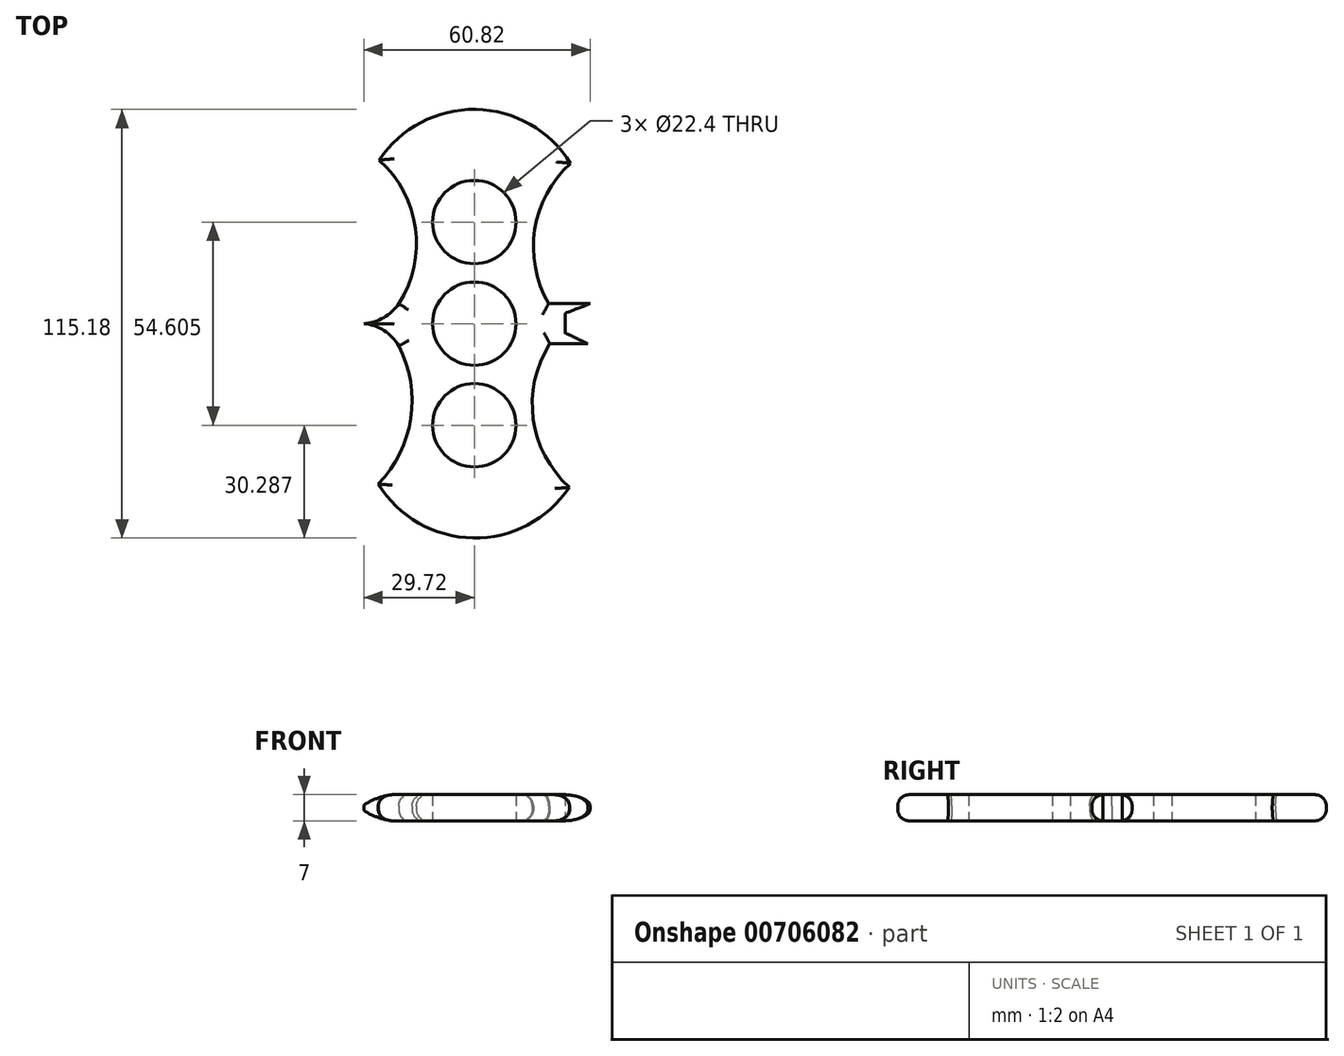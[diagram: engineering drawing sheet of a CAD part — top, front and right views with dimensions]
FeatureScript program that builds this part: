
annotation { "Feature Type Name" : "Feature", "Feature Type Description" : "" }
export const myFeature = defineFeature(function(context is Context, id is Id, definition is map)
    precondition{}
    {
        {
            var Q0;
            Q0=qCreatedBy(makeId("Top.planeOp"),FACE);
            var sketch = newSketch(context, id + "F0", { "sketchPlane" : qUnion([Q0])});
            skCircle(sketch, "E0", {"center": v(0, 0) * mm, "radius": 11.2 * mm});
            skCircle(sketch, "E1", {"center": v(0, 27.3) * mm, "radius": 11.2 * mm});
            skCircle(sketch, "E2.1.0", {"center": v(0, -27.3) * mm, "radius": 11.2 * mm});
            skArc(sketch, "E3", {"start": v(25.84, 43.07) * mm, "mid": v(0.39, 57.59) * mm, "end": v(-25.55, 43.95) * mm});
            skArc(sketch, "E4", {"start": v(-20.3, 5.4) * mm, "mid": v(-15.84, 25.64) * mm, "end": v(-25.55, 43.95) * mm});
            skArc(sketch, "E5.1.0", {"start": v(20.3, -5.4) * mm, "mid": v(15.84, -25.64) * mm, "end": v(25.55, -43.95) * mm});
            skArc(sketch, "E6", {"start": v(-31.68, 0) * mm, "mid": v(-25.26, 1.17) * mm, "end": v(-20.3, 5.4) * mm});
            skArc(sketch, "E7", {"start": v(-20.3, -5.99) * mm, "mid": v(-25.13, -1.36) * mm, "end": v(-31.68, 0) * mm});
            skArc(sketch, "E8", {"start": v(25.84, 43.07) * mm, "mid": v(16.24, 25.27) * mm, "end": v(20, 5.4) * mm});
            skArc(sketch, "E9.1.0", {"start": v(-25.84, -43.07) * mm, "mid": v(-0.39, -57.59) * mm, "end": v(25.55, -43.95) * mm});
            skLineSegment(sketch, "E10", {"start": v(20, 5.4) * mm, "end": v(31.1, 5.4) * mm});
            skLineSegment(sketch, "E11", {"start": v(31.1, 5.4) * mm, "end": v(24.38, 2.77) * mm});
            skLineSegment(sketch, "E12", {"start": v(24.38, 2.77) * mm, "end": v(24.38, -2.48) * mm});
            skLineSegment(sketch, "E13", {"start": v(20.3, -5.4) * mm, "end": v(30.51, -5.4) * mm});
            skArc(sketch, "E14", {"start": v(-25.84, -43.07) * mm, "mid": v(-17.08, -25.42) * mm, "end": v(-20.3, -5.99) * mm});
            skLineSegment(sketch, "E15", {"start": v(24.38, -2.48) * mm, "end": v(30.51, -5.4) * mm});
            skSolve(sketch);
        }
        {
            var Q0;
            Q0=makeQuery(id+"F0.imprint","IMPRINT",FACE,{"disambiguationData":[TD([[makeQuery(id+"F0.imprint","IMPRINT",EDGE,{"derivedFrom":sQuery(id+"F0.wireOp",EDGE,"E0")}),-1.0]])]});
            var Q1;
            Q1=makeQuery(id+"F0.imprint","IMPRINT",FACE,{"disambiguationData":[TD([[makeQuery(id+"F0.imprint","IMPRINT",EDGE,{"derivedFrom":sQuery(id+"F0.wireOp",EDGE,"E2.1.0")}),-1.0]])]});
            extrude(context, id + "F1", {"entities" : qUnion([Q0, Q1]), "depth" : 7 * mm, "offsetDistance" : 25 * mm});
        }
        {
            var Q0;
            Q0=makeQuery(id+"F1.opExtrude","CAP_EDGE",EDGE,{"disambiguationData":[OSD([sQuery(id+"F0.wireOp",EDGE,"E13")])],"isStart":false});
            var Q1;
            Q1=makeQuery(id+"F1.opExtrude","CAP_EDGE",EDGE,{"disambiguationData":[OSD([sQuery(id+"F0.wireOp",EDGE,"E3")])],"isStart":false});
            var Q2;
            Q2=makeQuery(id+"F1.opExtrude","CAP_EDGE",EDGE,{"disambiguationData":[OSD([sQuery(id+"F0.wireOp",EDGE,"E9.1.0")])],"isStart":false});
            var Q3;
            Q3=makeQuery(id+"F1.opExtrude","CAP_EDGE",EDGE,{"disambiguationData":[OSD([sQuery(id+"F0.wireOp",EDGE,"E14")])],"isStart":false});
            var Q4;
            Q4=makeQuery(id+"F1.opExtrude","CAP_EDGE",EDGE,{"disambiguationData":[OSD([sQuery(id+"F0.wireOp",EDGE,"E4")])],"isStart":false});
            var Q5;
            Q5=makeQuery(id+"F1.opExtrude","CAP_EDGE",EDGE,{"disambiguationData":[OSD([sQuery(id+"F0.wireOp",EDGE,"E8")])],"isStart":false});
            var Q6;
            Q6=makeQuery(id+"F1.opExtrude","CAP_EDGE",EDGE,{"disambiguationData":[OSD([sQuery(id+"F0.wireOp",EDGE,"E10")])],"isStart":false});
            var Q7;
            Q7=makeQuery(id+"F1.opExtrude","CAP_EDGE",EDGE,{"disambiguationData":[OSD([sQuery(id+"F0.wireOp",EDGE,"E5.1.0")])],"isStart":false});
            var Q8;
            Q8=makeQuery(id+"F1.opExtrude","CAP_EDGE",EDGE,{"disambiguationData":[OSD([sQuery(id+"F0.wireOp",EDGE,"E9.1.0")])],"isStart":true});
            var Q9;
            Q9=makeQuery(id+"F1.opExtrude","CAP_EDGE",EDGE,{"disambiguationData":[OSD([sQuery(id+"F0.wireOp",EDGE,"E3")])],"isStart":true});
            var Q10;
            Q10=makeQuery(id+"F1.opExtrude","CAP_EDGE",EDGE,{"disambiguationData":[OSD([sQuery(id+"F0.wireOp",EDGE,"E8")])],"isStart":true});
            var Q11;
            Q11=makeQuery(id+"F1.opExtrude","CAP_EDGE",EDGE,{"disambiguationData":[OSD([sQuery(id+"F0.wireOp",EDGE,"E14")])],"isStart":true});
            var Q12;
            Q12=makeQuery(id+"F1.opExtrude","CAP_EDGE",EDGE,{"disambiguationData":[OSD([sQuery(id+"F0.wireOp",EDGE,"E4")])],"isStart":true});
            var Q13;
            Q13=makeQuery(id+"F1.opExtrude","CAP_EDGE",EDGE,{"disambiguationData":[OSD([sQuery(id+"F0.wireOp",EDGE,"E10")])],"isStart":true});
            var Q14;
            Q14=makeQuery(id+"F1.opExtrude","CAP_EDGE",EDGE,{"disambiguationData":[OSD([sQuery(id+"F0.wireOp",EDGE,"E13")])],"isStart":true});
            var Q15;
            Q15=makeQuery(id+"F1.opExtrude","CAP_EDGE",EDGE,{"disambiguationData":[OSD([sQuery(id+"F0.wireOp",EDGE,"E5.1.0")])],"isStart":true});
            fillet(context, id + "F2", {"entities" : qUnion([Q0, Q1, Q2, Q3, Q4, Q5, Q6, Q7, Q8, Q9, Q10, Q11, Q12, Q13, Q14, Q15]), "radius" : 3 * mm, "tangentPropagation" : true, "allowEdgeOverflow" : false});
        }
    });
